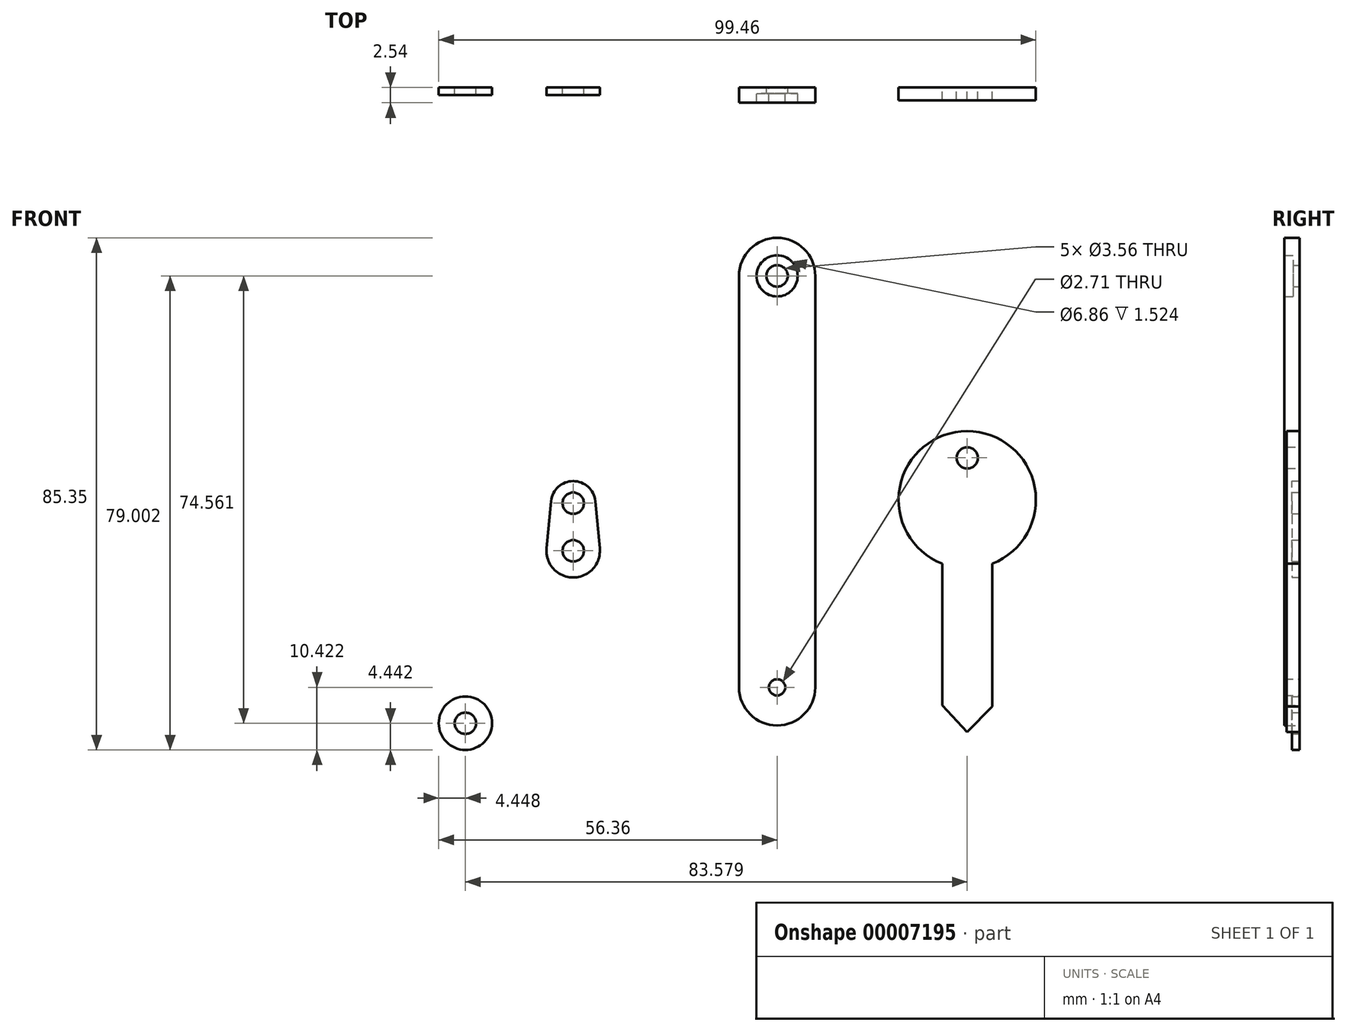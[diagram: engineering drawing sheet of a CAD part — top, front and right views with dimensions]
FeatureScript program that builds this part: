
annotation { "Feature Type Name" : "Feature", "Feature Type Description" : "" }
export const myFeature = defineFeature(function(context is Context, id is Id, definition is map)
    precondition{}
    {
        {
            var Q0;
            Q0=qCreatedBy(makeId("Front.planeOp"),FACE);
            var sketch = newSketch(context, id + "F0", { "sketchPlane" : qUnion([Q0])});
            skCircle(sketch, "E0", {"center": v(0, 40.98) * mm, "radius": 1.78 * mm});
            skCircle(sketch, "E1", {"center": v(0, -27.6) * mm, "radius": 1.35 * mm});
            skLineSegment(sketch, "E2", {"start": v(0, 40.98) * mm, "end": v(0, -27.6) * mm, "construction": true});
            skLineSegment(sketch, "E3", {"start": v(0, -27.6) * mm, "end": v(-36.93, -27.6) * mm, "construction": true});
            skLineSegment(sketch, "E4", {"start": v(0, 40.98) * mm, "end": v(-40.4, 40.98) * mm, "construction": true});
            skArc(sketch, "E5", {"start": v(6.35, 40.98) * mm, "mid": v(0, 47.33) * mm, "end": v(-6.35, 40.98) * mm});
            skArc(sketch, "E6", {"start": v(-6.35, -27.6) * mm, "mid": v(0, -33.95) * mm, "end": v(6.35, -27.6) * mm});
            skLineSegment(sketch, "E7", {"start": v(-6.35, 40.98) * mm, "end": v(-6.35, -27.6) * mm});
            skLineSegment(sketch, "E8", {"start": v(0, 40.98) * mm, "end": v(17.62, 40.98) * mm, "construction": true});
            skLineSegment(sketch, "E9", {"start": v(0, -27.6) * mm, "end": v(13.18, -27.6) * mm, "construction": true});
            skLineSegment(sketch, "E10", {"start": v(6.35, -27.6) * mm, "end": v(6.35, 40.98) * mm});
            skCircle(sketch, "E11", {"center": v(0, 40.98) * mm, "radius": 3.43 * mm});
            skSolve(sketch);
        }
        {
            var Q0;
            Q0=makeQuery(id+"F0.imprint","IMPRINT",FACE,{"disambiguationData":[TD([[makeQuery(id+"F0.imprint","IMPRINT",EDGE,{"derivedFrom":sQuery(id+"F0.wireOp",EDGE,"E0")}),-1.0]])]});
            extrude(context, id + "F1", {"entities" : qUnion([Q0]), "depth" : 1.02 * mm});
        }
        {
            var Q0;
            Q0=makeQuery(id+"F0.imprint","IMPRINT",FACE,{"disambiguationData":[TD([[makeQuery(id+"F0.imprint","IMPRINT",EDGE,{"derivedFrom":sQuery(id+"F0.wireOp",EDGE,"E1")}),-1.0]])]});
            extrude(context, id + "F2", {"entities" : qUnion([Q0]), "operationType" : NewBodyOperationType.ADD, "depth" : 2.54 * mm});
        }
        {
            var Q0;
            Q0=qCreatedBy(makeId("Front.planeOp"),FACE);
            var sketch = newSketch(context, id + "F3", { "sketchPlane" : qUnion([Q0])});
            skLineSegment(sketch, "E12", {"start": v(-33.96, -4.84) * mm, "end": v(-33.96, 3.1) * mm, "construction": true});
            skCircle(sketch, "E13", {"center": v(-33.96, 3.1) * mm, "radius": 1.78 * mm});
            skCircle(sketch, "E14", {"center": v(-33.96, -4.84) * mm, "radius": 1.78 * mm});
            skLineSegment(sketch, "E15", {"start": v(-37.62, 3.45) * mm, "end": v(-38.38, -4.41) * mm});
            skLineSegment(sketch, "E16", {"start": v(-30.3, 3.45) * mm, "end": v(-29.53, -4.41) * mm});
            skArc(sketch, "E17.trimOffspring", {"start": v(-38.38, -4.41) * mm, "mid": v(-33.96, -9.28) * mm, "end": v(-29.53, -4.41) * mm});
            skArc(sketch, "E18.trimOffspring", {"start": v(-30.3, 3.45) * mm, "mid": v(-33.96, 6.78) * mm, "end": v(-37.62, 3.45) * mm});
            skSolve(sketch);
        }
        {
            var Q0;
            Q0=makeQuery(id+"F3.imprint","IMPRINT",FACE,{"disambiguationData":[TD([[makeQuery(id+"F3.imprint","IMPRINT",EDGE,{"derivedFrom":sQuery(id+"F3.wireOp",EDGE,"E13")}),-1.0]])]});
            extrude(context, id + "F4", {"entities" : qUnion([Q0]), "depth" : 1.27 * mm});
        }
        {
            var Q0;
            Q0=qCreatedBy(makeId("Front.planeOp"),FACE);
            var sketch = newSketch(context, id + "F5", { "sketchPlane" : qUnion([Q0])});
            skCircle(sketch, "E19", {"center": v(-51.91, -33.58) * mm, "radius": 1.78 * mm});
            skCircle(sketch, "E20", {"center": v(-51.91, -33.58) * mm, "radius": 4.45 * mm});
            skSolve(sketch);
        }
        {
            var Q0;
            Q0=makeQuery(id+"F5.imprint","IMPRINT",FACE,{"disambiguationData":[TD([[makeQuery(id+"F5.imprint","IMPRINT",EDGE,{"derivedFrom":sQuery(id+"F5.wireOp",EDGE,"E19")}),-1.0]])]});
            extrude(context, id + "F6", {"entities" : qUnion([Q0]), "depth" : 1.27 * mm});
        }
        {
            var Q0;
            Q0=qCreatedBy(makeId("Front.planeOp"),FACE);
            var sketch = newSketch(context, id + "F7", { "sketchPlane" : qUnion([Q0])});
            skCircle(sketch, "E21", {"center": v(31.67, 10.65) * mm, "radius": 1.78 * mm});
            skLineSegment(sketch, "E22", {"start": v(31.67, 10.65) * mm, "end": v(31.67, -35.07) * mm, "construction": true});
            skLineSegment(sketch, "E23", {"start": v(27.51, -6.99) * mm, "end": v(27.51, -30.59) * mm});
            skLineSegment(sketch, "E24", {"start": v(35.82, -6.99) * mm, "end": v(35.82, -30.79) * mm});
            skLineSegment(sketch, "E25", {"start": v(27.51, -30.59) * mm, "end": v(31.67, -35.07) * mm});
            skLineSegment(sketch, "E26", {"start": v(31.67, -35.07) * mm, "end": v(35.82, -30.79) * mm});
            skArc(sketch, "E27", {"start": v(35.82, -6.99) * mm, "mid": v(31.67, 15.1) * mm, "end": v(27.51, -6.99) * mm});
            skPoint(sketch, "E28.orphan", {"position": v(27.51, 0) * mm});
            skPoint(sketch, "E29.orphan", {"position": v(35.82, 0) * mm});
            skSolve(sketch);
        }
        {
            var Q0;
            Q0=makeQuery(id+"F7.imprint","IMPRINT",FACE,{"disambiguationData":[TD([[makeQuery(id+"F7.imprint","IMPRINT",EDGE,{"derivedFrom":sQuery(id+"F7.wireOp",EDGE,"E21")}),-1.0]])]});
            extrude(context, id + "F8", {"entities" : qUnion([Q0]), "depth" : 2.16 * mm});
        }
    });
